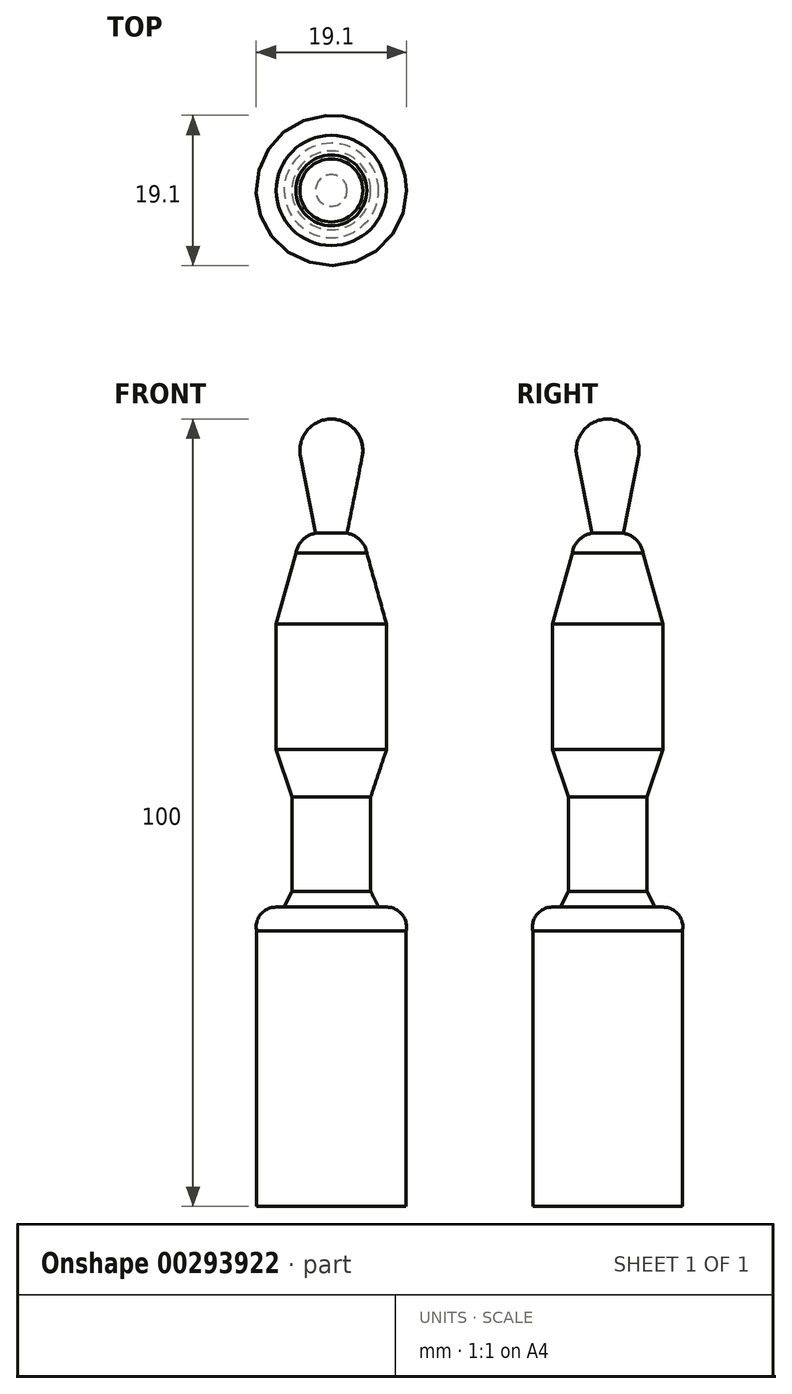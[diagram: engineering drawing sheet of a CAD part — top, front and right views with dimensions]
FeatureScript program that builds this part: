
annotation { "Feature Type Name" : "Feature", "Feature Type Description" : "" }
export const myFeature = defineFeature(function(context is Context, id is Id, definition is map)
    precondition{}
    {
        {
            var Q0;
            Q0=qCreatedBy(makeId("Front.planeOp"),FACE);
            var sketch = newSketch(context, id + "F0", { "sketchPlane" : qUnion([Q0])});
            skLineSegment(sketch, "E0", {"start": v(0, 0) * mm, "end": v(0, -100) * mm});
            skArc(sketch, "E1", {"start": v(4.5, -17) * mm, "mid": v(3.65, -15.35) * mm, "end": v(2, -14.5) * mm});
            skLineSegment(sketch, "E2", {"start": v(4.5, -17) * mm, "end": v(7, -26) * mm});
            skLineSegment(sketch, "E3", {"start": v(7, -26) * mm, "end": v(7, -42) * mm});
            skLineSegment(sketch, "E4", {"start": v(7, -42) * mm, "end": v(5, -48) * mm});
            skLineSegment(sketch, "E5", {"start": v(5, -48) * mm, "end": v(5, -60) * mm});
            skLineSegment(sketch, "E6", {"start": v(5, -60) * mm, "end": v(6, -62) * mm});
            skLineSegment(sketch, "E7", {"start": v(6, -62) * mm, "end": v(7.05, -62) * mm});
            skArc(sketch, "E8", {"start": v(9.5, -65) * mm, "mid": v(8.99, -62.92) * mm, "end": v(7.05, -62) * mm});
            skLineSegment(sketch, "E9", {"start": v(9.5, -65) * mm, "end": v(9.5, -100) * mm});
            skLineSegment(sketch, "E10", {"start": v(0, -100) * mm, "end": v(9.5, -100) * mm});
            skLineSegment(sketch, "E11", {"start": v(2, -14.5) * mm, "end": v(3.92, -4.78) * mm});
            skArc(sketch, "E12", {"start": v(3.92, -4.78) * mm, "mid": v(3.1, -1.46) * mm, "end": v(0, 0) * mm});
            skSolve(sketch);
        }
        {
            var Q0;
            Q0 = qSketchRegion(id + "F0", true);
            var Q1;
            Q1=sQuery(id+"F0.wireOp",EDGE,"E0");
            revolve(context, id + "F1", {"entities" : qUnion([Q0]), "axis" : qUnion([Q1]), "revolveType" : RevolveType.FULL});
        }
    });
